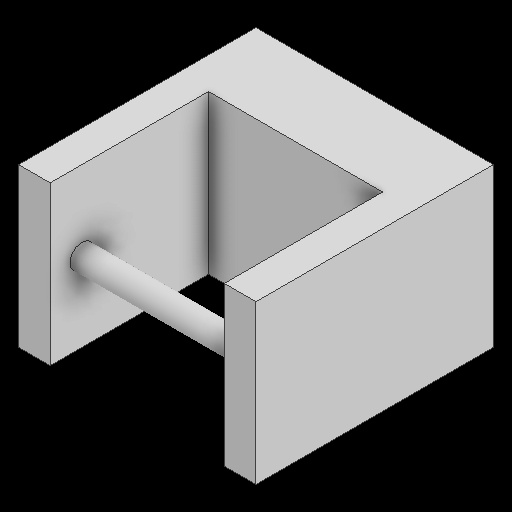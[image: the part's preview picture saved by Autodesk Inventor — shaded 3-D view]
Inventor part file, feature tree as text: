
AUTODESK INVENTOR PART (.ipt)
format: ipt  version: 2025.1 (Build 291241000, 241)  size: 121,856 bytes
history: native  units: in
note: dims shown in document units (in); Inventor stores cm internally (conversion verified against a paired STEP export)
features: extrude x3, sketch x3, projected_geometry x2, other x1
ambient origin geometry x8: Origin, YZ Plane, XZ Plane, XY Plane, X Axis, Y Axis, Z Axis, Center Point
bodies: Body1 (feature_tree)
feature tree (9):
  other  "솔리드1"
  extrude  "돌출1"  Depth=5.9055in
  extrude  "돌출2"  Depth=3.937in
  extrude  "돌출3"  Depth=1.9685in TaperAngle=0.0deg
  sketch  "스케치1"
  sketch  "스케치2"
  projected_geometry  "투영된 루프1"
  sketch  "스케치3"
  projected_geometry  "투영된 루프2"
